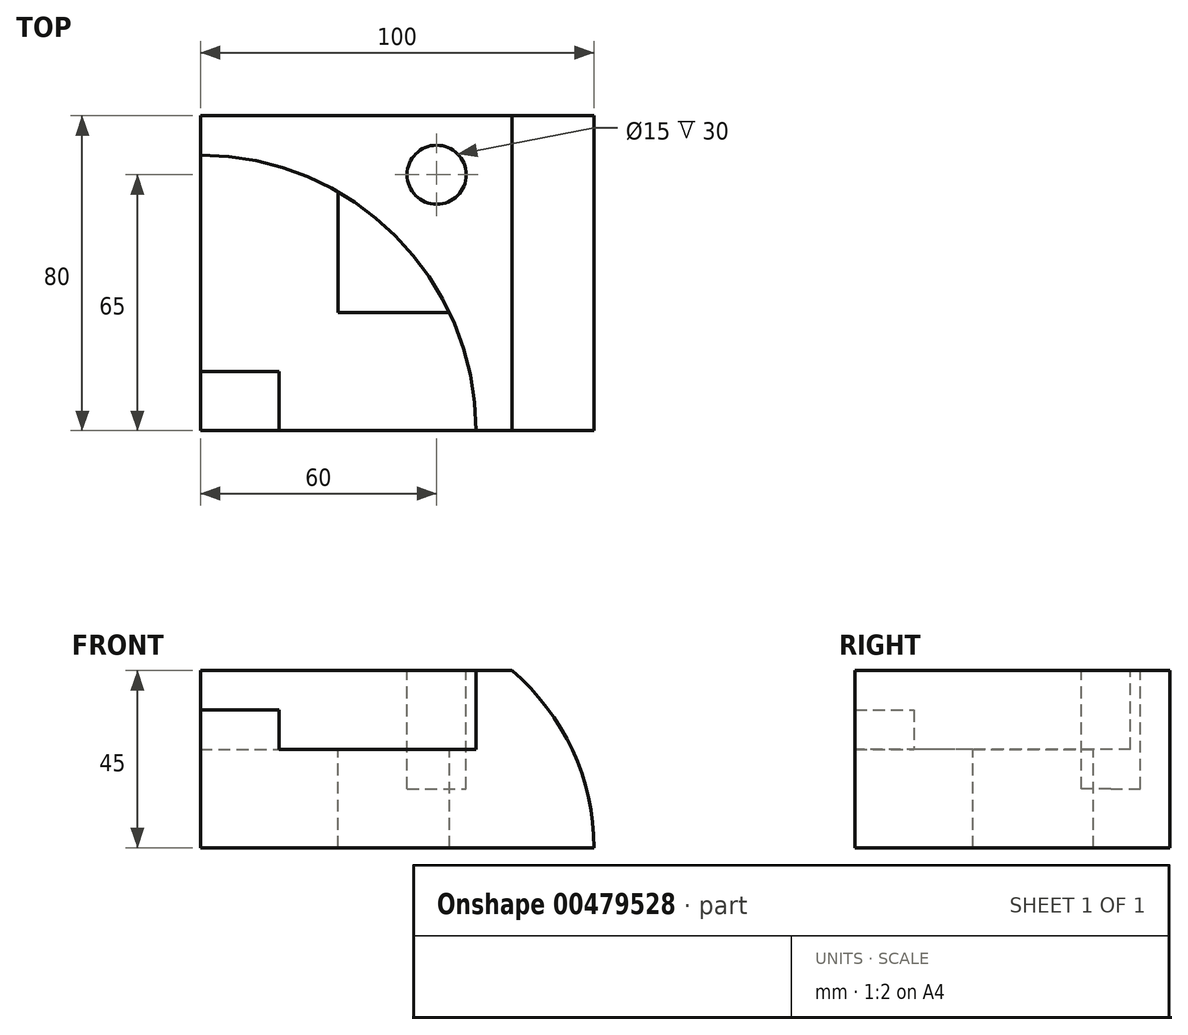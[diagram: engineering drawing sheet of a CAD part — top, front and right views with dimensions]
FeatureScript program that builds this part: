
annotation { "Feature Type Name" : "Feature", "Feature Type Description" : "" }
export const myFeature = defineFeature(function(context is Context, id is Id, definition is map)
    precondition{}
    {
        {
            var Q0;
            Q0=qCreatedBy(makeId("Top.planeOp"),FACE);
            var sketch = newSketch(context, id + "F0", { "sketchPlane" : qUnion([Q0])});
            skLineSegment(sketch, "E0.bottom", {"start": v(0, 0) * mm, "end": v(100, 0) * mm});
            skLineSegment(sketch, "E0.top", {"start": v(0, 80) * mm, "end": v(100, 80) * mm});
            skLineSegment(sketch, "E0.left", {"start": v(0, 0) * mm, "end": v(0, 80) * mm});
            skLineSegment(sketch, "E0.right", {"start": v(100, 0) * mm, "end": v(100, 80) * mm});
            skSolve(sketch);
        }
        {
            var Q0;
            Q0 = qSketchRegion(id + "F0", true);
            extrude(context, id + "F1", {"entities" : qUnion([Q0]), "depth" : 45 * mm});
        }
        {
            var Q0;
            Q0=makeQuery(id+"F1.opExtrude","CAP_FACE",FACE,{"disambiguationData":[OSD([sQuery(id+"F0.wireOp",EDGE,"E0.bottom"),sQuery(id+"F0.wireOp",EDGE,"E0.top"),sQuery(id+"F0.wireOp",EDGE,"E0.left"),sQuery(id+"F0.wireOp",EDGE,"E0.right")])],"isStart":true});
            cPlane(context, id + "F2", {"entities" : qUnion([Q0]), "cplaneType" : CPlaneType.OFFSET, "offset" : 25 * mm, "oppositeDirection" : true, "width" : 150 * mm, "height" : 150 * mm});
        }
        {
            var Q0;
            Q0=qCreatedBy(id+"F2.planeOp",FACE);
            cPlane(context, id + "F3", {"entities" : qUnion([Q0]), "cplaneType" : CPlaneType.OFFSET, "offset" : 10 * mm, "oppositeDirection" : true, "width" : 150 * mm, "height" : 150 * mm});
        }
        {
            var Q0;
            Q0=makeQuery(id+"F1.opExtrude","CAP_FACE",FACE,{"disambiguationData":[OSD([sQuery(id+"F0.wireOp",EDGE,"E0.bottom"),sQuery(id+"F0.wireOp",EDGE,"E0.top"),sQuery(id+"F0.wireOp",EDGE,"E0.left"),sQuery(id+"F0.wireOp",EDGE,"E0.right")])],"isStart":true});
            cPlane(context, id + "F4", {"entities" : qUnion([Q0]), "cplaneType" : CPlaneType.OFFSET, "offset" : 15 * mm, "oppositeDirection" : true, "width" : 150 * mm, "height" : 150 * mm});
        }
        {
            var Q0;
            Q0=makeQuery(id+"F1.opExtrude","CAP_FACE",FACE,{"disambiguationData":[OSD([sQuery(id+"F0.wireOp",EDGE,"E0.bottom"),sQuery(id+"F0.wireOp",EDGE,"E0.top"),sQuery(id+"F0.wireOp",EDGE,"E0.left"),sQuery(id+"F0.wireOp",EDGE,"E0.right")])],"isStart":false});
            var sketch = newSketch(context, id + "F5", { "sketchPlane" : qUnion([Q0])});
            skCircle(sketch, "E1", {"center": v(60, 65) * mm, "radius": 7.5 * mm});
            skSolve(sketch);
        }
        {
            var Q0;
            Q0 = qSketchRegion(id + "F5", true);
            var Q1;
            Q1=qCreatedBy(id+"F4.planeOp",FACE);
            extrude(context, id + "F6", {"entities" : qUnion([Q0]), "operationType" : NewBodyOperationType.REMOVE, "endBound" : BoundingType.UP_TO_SURFACE, "oppositeDirection" : true, "endBoundEntityFace" : qUnion([Q1]), "depth" : 25 * mm});
        }
        {
            var Q0;
            Q0=makeQuery(id+"F1.opExtrude","SWEPT_FACE",FACE,{"disambiguationData":[OSD([sQuery(id+"F0.wireOp",EDGE,"E0.bottom")])]});
            var sketch = newSketch(context, id + "F7", { "sketchPlane" : qUnion([Q0])});
            skCircle(sketch, "E2", {"center": v(41.1, 0) * mm, "radius": 58.9 * mm});
            skSolve(sketch);
        }
        {
            var Q0;
            {var subQ1=sQuery(id+"F0.wireOp",EDGE,"E0.bottom");var subQ2=makeQuery(id+"F1.opExtrude","SWEPT_EDGE",EDGE,{"disambiguationData":[OSD([subQ1,sQuery(id+"F0.wireOp",EDGE,"E0.right")])]});Q0=makeQuery(id+"F7.imprint","IMPRINT",FACE,{"disambiguationData":[TD([[makeQuery(id+"F7.imprint","IMPRINT",EDGE,{"derivedFrom":subQ2}),-1.0]])]});}
            extrude(context, id + "F8", {"entities" : qUnion([Q0]), "operationType" : NewBodyOperationType.REMOVE, "endBound" : BoundingType.THROUGH_ALL, "oppositeDirection" : true, "depth" : 25 * mm});
        }
        {
            var Q0;
            Q0=makeQuery(id+"F1.opExtrude","CAP_FACE",FACE,{"disambiguationData":[OSD([sQuery(id+"F0.wireOp",EDGE,"E0.bottom"),sQuery(id+"F0.wireOp",EDGE,"E0.top"),sQuery(id+"F0.wireOp",EDGE,"E0.left"),sQuery(id+"F0.wireOp",EDGE,"E0.right")])],"isStart":false});
            var sketch = newSketch(context, id + "F9", { "sketchPlane" : qUnion([Q0])});
            skCircle(sketch, "E3", {"center": v(0, 0) * mm, "radius": 70 * mm});
            skSolve(sketch);
        }
        {
            var Q0;
            Q0 = qSketchRegion(id + "F9", true);
            var Q1;
            Q1=qCreatedBy(id+"F2.planeOp",FACE);
            extrude(context, id + "F10", {"entities" : qUnion([Q0]), "operationType" : NewBodyOperationType.REMOVE, "endBound" : BoundingType.UP_TO_SURFACE, "oppositeDirection" : true, "endBoundEntityFace" : qUnion([Q1]), "depth" : 25 * mm});
        }
        {
            var Q0;
            Q0=makeQuery(id+"F10.boolean.opBoolean","COPY",FACE,{"derivedFrom":makeQuery(id+"F10.opExtrude","CAP_FACE",FACE,{"disambiguationData":[OSD([sQuery(id+"F9.wireOp",EDGE,"E3")])],"isStart":false})});
            var sketch = newSketch(context, id + "F11", { "sketchPlane" : qUnion([Q0])});
            skLineSegment(sketch, "E4.bottom", {"start": v(0, 0) * mm, "end": v(20, 0) * mm});
            skLineSegment(sketch, "E4.top", {"start": v(0, 15) * mm, "end": v(20, 15) * mm});
            skLineSegment(sketch, "E4.left", {"start": v(0, 0) * mm, "end": v(0, 15) * mm});
            skLineSegment(sketch, "E4.right", {"start": v(20, 0) * mm, "end": v(20, 15) * mm});
            skSolve(sketch);
        }
        {
            var Q0;
            Q0 = qSketchRegion(id + "F11", true);
            var Q1;
            Q1=qCreatedBy(id+"F3.planeOp",FACE);
            extrude(context, id + "F12", {"entities" : qUnion([Q0]), "operationType" : NewBodyOperationType.ADD, "endBound" : BoundingType.UP_TO_SURFACE, "endBoundEntityFace" : qUnion([Q1]), "depth" : 25 * mm});
        }
        {
            var Q0;
            Q0=makeQuery(id+"F10.boolean.opBoolean","COPY",FACE,{"derivedFrom":makeQuery(id+"F10.opExtrude","CAP_FACE",FACE,{"disambiguationData":[OSD([sQuery(id+"F9.wireOp",EDGE,"E3")])],"isStart":false})});
            var sketch = newSketch(context, id + "F13", { "sketchPlane" : qUnion([Q0])});
            skLineSegment(sketch, "E5", {"start": v(63.25, 30) * mm, "end": v(35, 30) * mm});
            skLineSegment(sketch, "E6", {"start": v(35, 30) * mm, "end": v(35, 60.62) * mm});
            skSolve(sketch);
        }
        {
            var Q0;
            Q0 = qSketchRegion(id + "F13", true);
            var Q1;
            {var subQ0=sQuery(id+"F13.wireOp",EDGE,"E5");Q1=makeQuery(id+"F13.imprint","IMPRINT",FACE,{"disambiguationData":[TD([[makeQuery(id+"F13.imprint","IMPRINT",EDGE,{"derivedFrom":subQ0}),-1.0]])]});}
            extrude(context, id + "F14", {"entities" : qUnion([Q0, Q1]), "operationType" : NewBodyOperationType.REMOVE, "endBound" : BoundingType.THROUGH_ALL, "oppositeDirection" : true, "depth" : 25 * mm});
        }
    });
